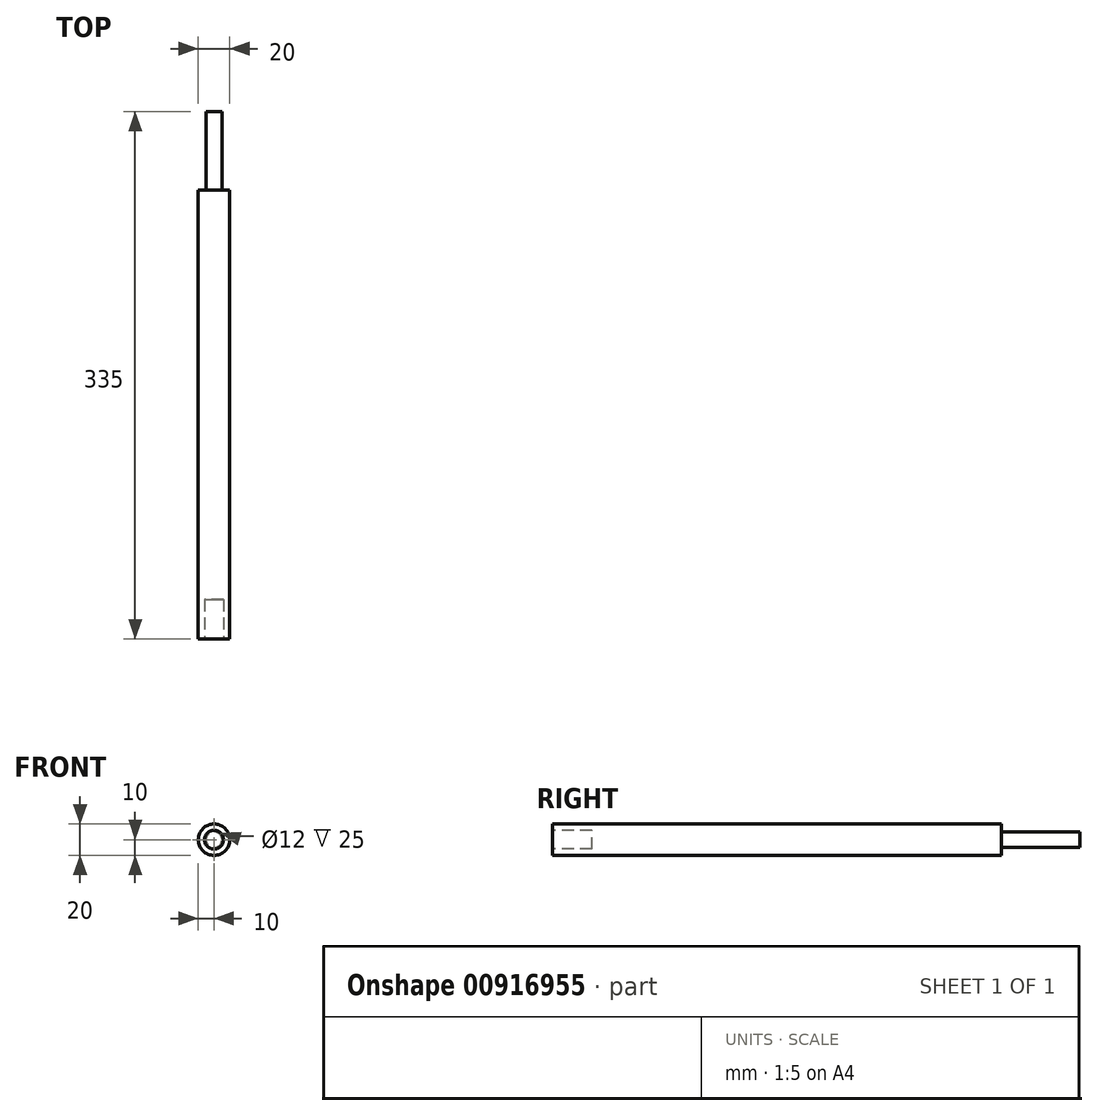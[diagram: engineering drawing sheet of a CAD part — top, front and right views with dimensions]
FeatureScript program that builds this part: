
annotation { "Feature Type Name" : "Feature", "Feature Type Description" : "" }
export const myFeature = defineFeature(function(context is Context, id is Id, definition is map)
    precondition{}
    {
        {
            var Q0;
            Q0=qCreatedBy(makeId("Front.planeOp"),FACE);
            var sketch = newSketch(context, id + "F0", { "sketchPlane" : qUnion([Q0])});
            skCircle(sketch, "E0", {"center": v(0, 0) * mm, "radius": 10 * mm});
            skSolve(sketch);
        }
        {
            var Q0;
            Q0=makeQuery(id+"F0.imprint","IMPRINT",FACE,{"disambiguationData":[TD([[makeQuery(id+"F0.imprint","IMPRINT",EDGE,{"derivedFrom":sQuery(id+"F0.wireOp",EDGE,"E0")}),1.0]])]});
            extrude(context, id + "F1", {"entities" : qUnion([Q0]), "depth" : 285 * mm, "offsetDistance" : 25 * mm});
        }
        {
            var Q0;
            Q0=makeQuery(id+"F1.opExtrude","CAP_FACE",FACE,{"disambiguationData":[OSD([sQuery(id+"F0.wireOp",EDGE,"E0")])],"isStart":false});
            var sketch = newSketch(context, id + "F2", { "sketchPlane" : qUnion([Q0])});
            skCircle(sketch, "E1", {"center": v(0, 0) * mm, "radius": 6 * mm});
            skSolve(sketch);
        }
        {
            var Q0;
            Q0=makeQuery(id+"F2.imprint","IMPRINT",FACE,{"disambiguationData":[TD([[makeQuery(id+"F2.imprint","IMPRINT",EDGE,{"derivedFrom":sQuery(id+"F2.wireOp",EDGE,"E1")}),1.0]])]});
            extrude(context, id + "F3", {"entities" : qUnion([Q0]), "operationType" : NewBodyOperationType.REMOVE, "oppositeDirection" : true, "depth" : 25 * mm, "offsetDistance" : 25 * mm});
        }
        {
            var Q0;
            Q0=makeQuery(id+"F1.opExtrude","CAP_FACE",FACE,{"disambiguationData":[OSD([sQuery(id+"F0.wireOp",EDGE,"E0")])],"isStart":true});
            var sketch = newSketch(context, id + "F4", { "sketchPlane" : qUnion([Q0])});
            skCircle(sketch, "E2", {"center": v(0, 0) * mm, "radius": 5 * mm});
            skSolve(sketch);
        }
        {
            var Q0;
            Q0=makeQuery(id+"F4.imprint","IMPRINT",FACE,{"disambiguationData":[TD([[makeQuery(id+"F4.imprint","IMPRINT",EDGE,{"derivedFrom":sQuery(id+"F4.wireOp",EDGE,"E2")}),1.0]])]});
            extrude(context, id + "F5", {"entities" : qUnion([Q0]), "operationType" : NewBodyOperationType.ADD, "depth" : 50 * mm, "offsetDistance" : 25 * mm});
        }
    });
